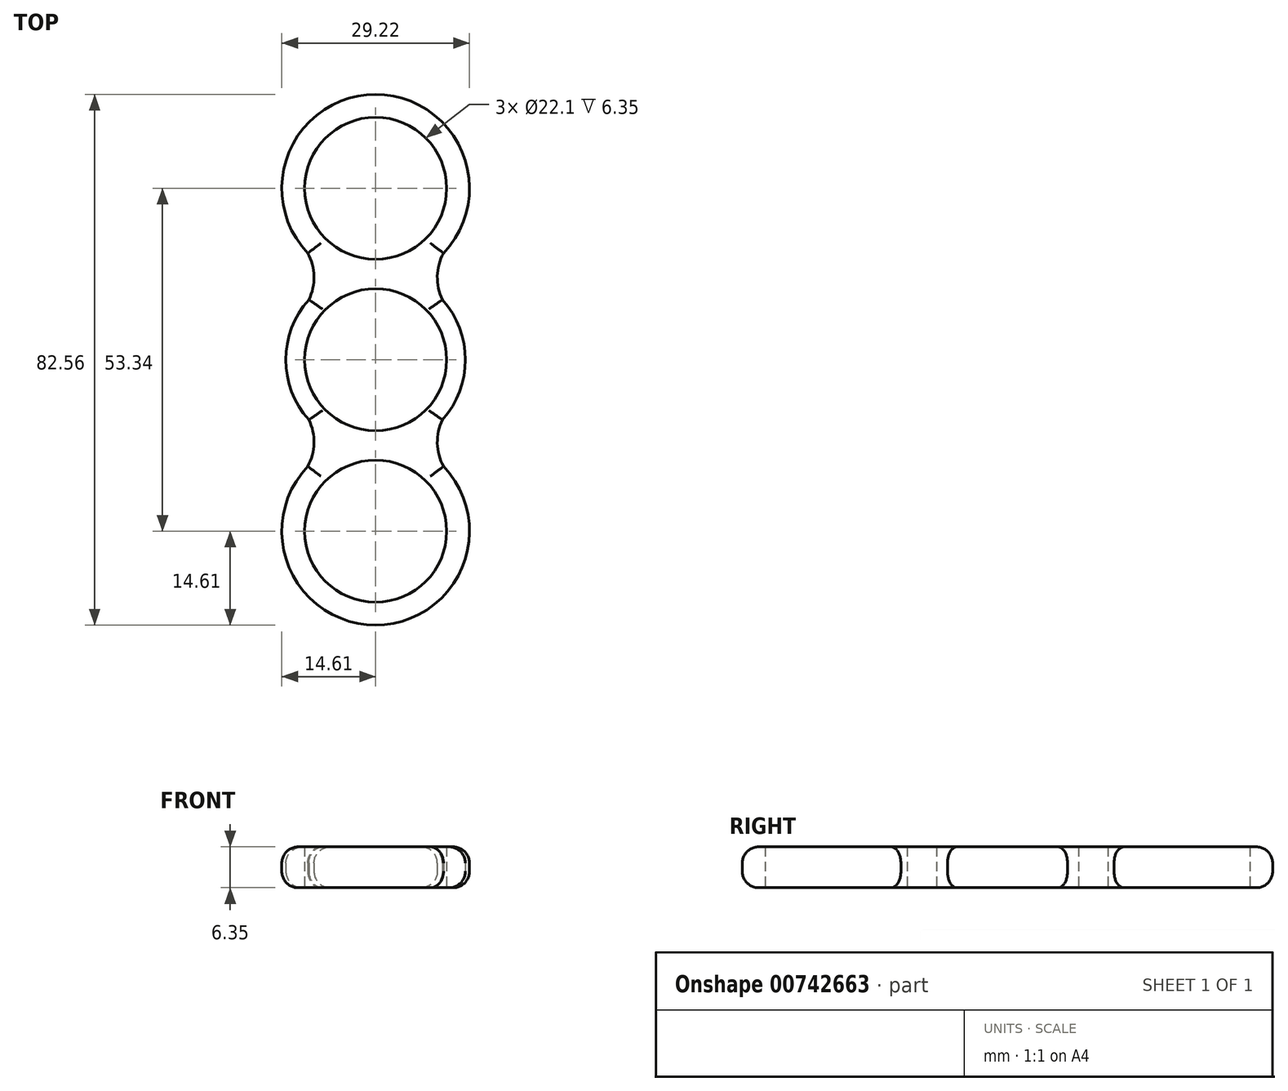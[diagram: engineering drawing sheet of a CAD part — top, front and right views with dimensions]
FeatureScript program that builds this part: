
annotation { "Feature Type Name" : "Feature", "Feature Type Description" : "" }
export const myFeature = defineFeature(function(context is Context, id is Id, definition is map)
    precondition{}
    {
        {
            var Q0;
            Q0=qCreatedBy(makeId("Top.planeOp"),FACE);
            var sketch = newSketch(context, id + "F0", { "sketchPlane" : qUnion([Q0])});
            skCircle(sketch, "E0", {"center": v(0, 0) * mm, "radius": 11.05 * mm});
            skArc(sketch, "E1", {"start": v(-10.4, 9.34) * mm, "mid": v(-13.97, 0) * mm, "end": v(-10.4, -9.34) * mm});
            skCircle(sketch, "E2", {"center": v(0, 26.67) * mm, "radius": 11.05 * mm});
            skArc(sketch, "E3", {"start": v(10.57, 16.59) * mm, "mid": v(0, 41.28) * mm, "end": v(-10.57, 16.59) * mm});
            skCircle(sketch, "E4.1.0", {"center": v(0, -26.67) * mm, "radius": 11.05 * mm});
            skArc(sketch, "E4.1.1", {"start": v(-10.57, -16.59) * mm, "mid": v(0, -41.28) * mm, "end": v(10.57, -16.59) * mm});
            skArc(sketch, "E5.trimOffspring", {"start": v(10.4, -9.34) * mm, "mid": v(13.97, 0) * mm, "end": v(10.4, 9.34) * mm});
            skArc(sketch, "E6", {"start": v(12.24, 18.7) * mm, "mid": v(9.6, 12.91) * mm, "end": v(12.06, 7.05) * mm});
            skArc(sketch, "E7", {"start": v(-12.06, 7.05) * mm, "mid": v(-9.6, 12.91) * mm, "end": v(-12.24, 18.7) * mm});
            skArc(sketch, "E8.1.0", {"start": v(-12.24, -18.7) * mm, "mid": v(-9.6, -12.91) * mm, "end": v(-12.06, -7.05) * mm});
            skArc(sketch, "E8.1.1", {"start": v(12.06, -7.05) * mm, "mid": v(9.6, -12.91) * mm, "end": v(12.24, -18.7) * mm});
            skSolve(sketch);
        }
        {
            var Q0;
            Q0 = qSketchRegion(id + "F0", true);
            extrude(context, id + "F1", {"entities" : qUnion([Q0]), "depth" : 6.35 * mm, "offsetDistance" : 25.4 * mm});
        }
        {
            var Q0;
            Q0=makeQuery(id+"F1.opExtrude","CAP_EDGE",EDGE,{"disambiguationData":[OSD([sQuery(id+"F0.wireOp",EDGE,"E3")])],"isStart":false});
            var Q1;
            Q1=makeQuery(id+"F1.opExtrude","CAP_EDGE",EDGE,{"disambiguationData":[OSD([sQuery(id+"F0.wireOp",EDGE,"E4.1.1")])],"isStart":false});
            var Q2;
            Q2=makeQuery(id+"F1.opExtrude","CAP_EDGE",EDGE,{"disambiguationData":[OSD([sQuery(id+"F0.wireOp",EDGE,"E8.1.1")])],"isStart":false});
            var Q3;
            Q3=makeQuery(id+"F1.opExtrude","CAP_EDGE",EDGE,{"disambiguationData":[OSD([sQuery(id+"F0.wireOp",EDGE,"E8.1.0")])],"isStart":false});
            var Q4;
            Q4=makeQuery(id+"F1.opExtrude","CAP_EDGE",EDGE,{"disambiguationData":[OSD([sQuery(id+"F0.wireOp",EDGE,"E1")])],"isStart":false});
            var Q5;
            Q5=makeQuery(id+"F1.opExtrude","CAP_EDGE",EDGE,{"disambiguationData":[OSD([sQuery(id+"F0.wireOp",EDGE,"E5.trimOffspring")])],"isStart":false});
            var Q6;
            Q6=makeQuery(id+"F1.opExtrude","CAP_EDGE",EDGE,{"disambiguationData":[OSD([sQuery(id+"F0.wireOp",EDGE,"E6")])],"isStart":false});
            var Q7;
            Q7=makeQuery(id+"F1.opExtrude","CAP_EDGE",EDGE,{"disambiguationData":[OSD([sQuery(id+"F0.wireOp",EDGE,"E7")])],"isStart":false});
            var Q8;
            Q8=makeQuery(id+"F1.opExtrude","CAP_EDGE",EDGE,{"disambiguationData":[OSD([sQuery(id+"F0.wireOp",EDGE,"E4.1.1")])],"isStart":true});
            var Q9;
            Q9=makeQuery(id+"F1.opExtrude","CAP_EDGE",EDGE,{"disambiguationData":[OSD([sQuery(id+"F0.wireOp",EDGE,"E8.1.1")])],"isStart":true});
            var Q10;
            Q10=makeQuery(id+"F1.opExtrude","CAP_EDGE",EDGE,{"disambiguationData":[OSD([sQuery(id+"F0.wireOp",EDGE,"E8.1.0")])],"isStart":true});
            var Q11;
            Q11=makeQuery(id+"F1.opExtrude","CAP_EDGE",EDGE,{"disambiguationData":[OSD([sQuery(id+"F0.wireOp",EDGE,"E5.trimOffspring")])],"isStart":true});
            var Q12;
            Q12=makeQuery(id+"F1.opExtrude","CAP_EDGE",EDGE,{"disambiguationData":[OSD([sQuery(id+"F0.wireOp",EDGE,"E1")])],"isStart":true});
            var Q13;
            Q13=makeQuery(id+"F1.opExtrude","CAP_EDGE",EDGE,{"disambiguationData":[OSD([sQuery(id+"F0.wireOp",EDGE,"E7")])],"isStart":true});
            var Q14;
            Q14=makeQuery(id+"F1.opExtrude","CAP_EDGE",EDGE,{"disambiguationData":[OSD([sQuery(id+"F0.wireOp",EDGE,"E3")])],"isStart":true});
            var Q15;
            Q15=makeQuery(id+"F1.opExtrude","CAP_EDGE",EDGE,{"disambiguationData":[OSD([sQuery(id+"F0.wireOp",EDGE,"E6")])],"isStart":true});
            fillet(context, id + "F2", {"entities" : qUnion([Q0, Q1, Q2, Q3, Q4, Q5, Q6, Q7, Q8, Q9, Q10, Q11, Q12, Q13, Q14, Q15]), "radius" : 2.54 * mm, "tangentPropagation" : true, "allowEdgeOverflow" : false});
        }
    });
